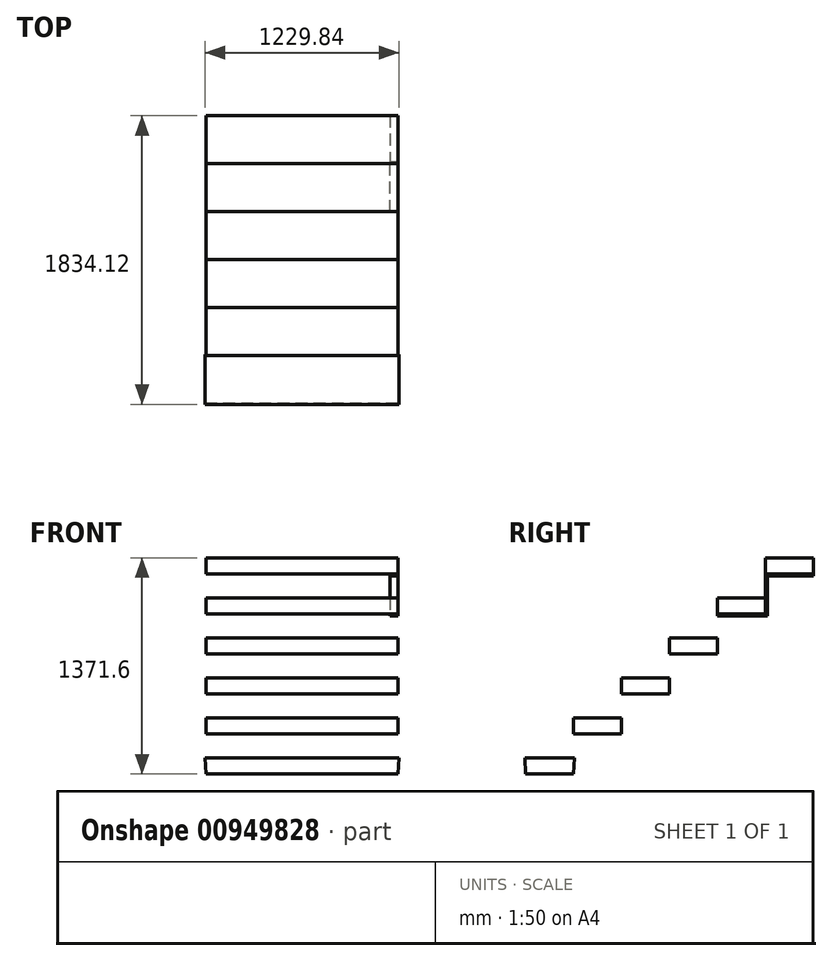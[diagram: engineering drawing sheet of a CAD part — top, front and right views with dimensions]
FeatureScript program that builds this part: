
annotation { "Feature Type Name" : "Feature", "Feature Type Description" : "" }
export const myFeature = defineFeature(function(context is Context, id is Id, definition is map)
    precondition{}
    {
        {
            var Q0;
            Q0=qCreatedBy(makeId("Top.planeOp"),FACE);
            var sketch = newSketch(context, id + "F0", { "sketchPlane" : qUnion([Q0])});
            skLineSegment(sketch, "E0.bottom", {"start": v(609.6, 152.4) * mm, "end": v(-609.6, 152.4) * mm});
            skLineSegment(sketch, "E0.top", {"start": v(609.6, -152.4) * mm, "end": v(-609.6, -152.4) * mm});
            skLineSegment(sketch, "E0.left", {"start": v(609.6, 152.4) * mm, "end": v(609.6, -152.4) * mm});
            skLineSegment(sketch, "E0.right", {"start": v(-609.6, 152.4) * mm, "end": v(-609.6, -152.4) * mm});
            skPoint(sketch, "E0.middle", {"position": v(0, 0) * mm});
            skSolve(sketch);
        }
        {
            var Q0;
            Q0 = qSketchRegion(id + "F0", true);
            extrude(context, id + "F1", {"entities" : qUnion([Q0]), "depth" : 101.6 * mm, "offsetDistance" : 25.4 * mm, "hasDraft" : true, "draftAngle" : 3 * degree});
        }
        {
            var Q0;
            Q0=makeQuery(id+"F1.opExtrude","CAP_FACE",FACE,{"disambiguationData":[OSD([sQuery(id+"F0.wireOp",EDGE,"E0.bottom"),sQuery(id+"F0.wireOp",EDGE,"E0.top"),sQuery(id+"F0.wireOp",EDGE,"E0.left"),sQuery(id+"F0.wireOp",EDGE,"E0.right")])],"isStart":false});
            cPlane(context, id + "F2", {"entities" : qUnion([Q0]), "cplaneType" : CPlaneType.OFFSET, "offset" : 152.4 * mm, "width" : 152.4 * mm, "height" : 152.4 * mm});
        }
        {
            var Q0;
            Q0=qCreatedBy(id+"F2.planeOp",FACE);
            var sketch = newSketch(context, id + "F3", { "sketchPlane" : qUnion([Q0])});
            skLineSegment(sketch, "E1.bottom", {"start": v(609.6, 457.2) * mm, "end": v(-609.6, 457.2) * mm});
            skLineSegment(sketch, "E1.top", {"start": v(609.6, 152.4) * mm, "end": v(-609.6, 152.4) * mm});
            skLineSegment(sketch, "E1.left", {"start": v(609.6, 457.2) * mm, "end": v(609.6, 152.4) * mm});
            skLineSegment(sketch, "E1.right", {"start": v(-609.6, 457.2) * mm, "end": v(-609.6, 152.4) * mm});
            skPoint(sketch, "E1.middle", {"position": v(0, 304.8) * mm});
            skSolve(sketch);
        }
        {
            var Q0;
            Q0 = qSketchRegion(id + "F3", true);
            extrude(context, id + "F4", {"entities" : qUnion([Q0]), "depth" : 101.6 * mm, "offsetDistance" : 25.4 * mm});
        }
        {
            var Q0;
            Q0=makeQuery(id+"F4.opExtrude","CAP_FACE",FACE,{"disambiguationData":[OSD([sQuery(id+"F3.wireOp",EDGE,"E1.bottom"),sQuery(id+"F3.wireOp",EDGE,"E1.top"),sQuery(id+"F3.wireOp",EDGE,"E1.left"),sQuery(id+"F3.wireOp",EDGE,"E1.right")])],"isStart":false});
            cPlane(context, id + "F5", {"entities" : qUnion([Q0]), "cplaneType" : CPlaneType.OFFSET, "offset" : 152.4 * mm, "width" : 152.4 * mm, "height" : 152.4 * mm});
        }
        {
            var Q0;
            Q0=qCreatedBy(id+"F5.planeOp",FACE);
            var sketch = newSketch(context, id + "F6", { "sketchPlane" : qUnion([Q0])});
            skLineSegment(sketch, "E2.bottom", {"start": v(609.6, 762) * mm, "end": v(-609.6, 762) * mm});
            skLineSegment(sketch, "E2.top", {"start": v(609.6, 457.2) * mm, "end": v(-609.6, 457.2) * mm});
            skLineSegment(sketch, "E2.left", {"start": v(609.6, 762) * mm, "end": v(609.6, 457.2) * mm});
            skLineSegment(sketch, "E2.right", {"start": v(-609.6, 762) * mm, "end": v(-609.6, 457.2) * mm});
            skPoint(sketch, "E2.middle", {"position": v(0, 609.6) * mm});
            skSolve(sketch);
        }
        {
            var Q0;
            Q0 = qSketchRegion(id + "F6", true);
            extrude(context, id + "F7", {"entities" : qUnion([Q0]), "depth" : 101.6 * mm, "offsetDistance" : 25.4 * mm});
        }
        {
            var Q0;
            Q0=makeQuery(id+"F7.opExtrude","CAP_FACE",FACE,{"disambiguationData":[OSD([sQuery(id+"F6.wireOp",EDGE,"E2.bottom"),sQuery(id+"F6.wireOp",EDGE,"E2.top"),sQuery(id+"F6.wireOp",EDGE,"E2.left"),sQuery(id+"F6.wireOp",EDGE,"E2.right")])],"isStart":false});
            cPlane(context, id + "F8", {"entities" : qUnion([Q0]), "cplaneType" : CPlaneType.OFFSET, "offset" : 152.4 * mm, "width" : 152.4 * mm, "height" : 152.4 * mm});
        }
        {
            var Q0;
            Q0=qCreatedBy(id+"F8.planeOp",FACE);
            var sketch = newSketch(context, id + "F9", { "sketchPlane" : qUnion([Q0])});
            skLineSegment(sketch, "E3.bottom", {"start": v(609.6, 1066.8) * mm, "end": v(-609.6, 1066.8) * mm});
            skLineSegment(sketch, "E3.top", {"start": v(609.6, 762) * mm, "end": v(-609.6, 762) * mm});
            skLineSegment(sketch, "E3.left", {"start": v(609.6, 1066.8) * mm, "end": v(609.6, 762) * mm});
            skLineSegment(sketch, "E3.right", {"start": v(-609.6, 1066.8) * mm, "end": v(-609.6, 762) * mm});
            skPoint(sketch, "E3.middle", {"position": v(0, 914.4) * mm});
            skSolve(sketch);
        }
        {
            var Q0;
            Q0=makeQuery(id+"F9.imprint","IMPRINT",FACE,{"disambiguationData":[TD([[makeQuery(id+"F9.imprint","IMPRINT",EDGE,{"derivedFrom":sQuery(id+"F9.wireOp",EDGE,"E3.bottom")}),1.0]])]});
            extrude(context, id + "F10", {"entities" : qUnion([Q0]), "depth" : 101.6 * mm, "offsetDistance" : 25.4 * mm});
        }
        {
            var Q0;
            Q0=makeQuery(id+"F10.opExtrude","CAP_FACE",FACE,{"disambiguationData":[OSD([sQuery(id+"F9.wireOp",EDGE,"E3.bottom"),sQuery(id+"F9.wireOp",EDGE,"E3.top"),sQuery(id+"F9.wireOp",EDGE,"E3.left"),sQuery(id+"F9.wireOp",EDGE,"E3.right")])],"isStart":false});
            cPlane(context, id + "F11", {"entities" : qUnion([Q0]), "cplaneType" : CPlaneType.OFFSET, "offset" : 152.4 * mm, "width" : 152.4 * mm, "height" : 152.4 * mm});
        }
        {
            var Q0;
            Q0=qCreatedBy(id+"F11.planeOp",FACE);
            var sketch = newSketch(context, id + "F12", { "sketchPlane" : qUnion([Q0])});
            skLineSegment(sketch, "E4.bottom", {"start": v(609.6, 1371.6) * mm, "end": v(-609.6, 1371.6) * mm});
            skLineSegment(sketch, "E4.top", {"start": v(609.6, 1066.8) * mm, "end": v(-609.6, 1066.8) * mm});
            skLineSegment(sketch, "E4.left", {"start": v(609.6, 1371.6) * mm, "end": v(609.6, 1066.8) * mm});
            skLineSegment(sketch, "E4.right", {"start": v(-609.6, 1371.6) * mm, "end": v(-609.6, 1066.8) * mm});
            skPoint(sketch, "E4.middle", {"position": v(0, 1219.2) * mm});
            skSolve(sketch);
        }
        {
            var Q0;
            Q0=makeQuery(id+"F12.imprint","IMPRINT",FACE,{"disambiguationData":[TD([[makeQuery(id+"F12.imprint","IMPRINT",EDGE,{"derivedFrom":sQuery(id+"F12.wireOp",EDGE,"E4.bottom")}),1.0]])]});
            extrude(context, id + "F13", {"entities" : qUnion([Q0]), "depth" : 101.6 * mm, "offsetDistance" : 25.4 * mm});
        }
        {
            var Q0;
            Q0=makeQuery(id+"F13.opExtrude","CAP_FACE",FACE,{"disambiguationData":[OSD([sQuery(id+"F12.wireOp",EDGE,"E4.bottom"),sQuery(id+"F12.wireOp",EDGE,"E4.top"),sQuery(id+"F12.wireOp",EDGE,"E4.left"),sQuery(id+"F12.wireOp",EDGE,"E4.right")])],"isStart":false});
            cPlane(context, id + "F14", {"entities" : qUnion([Q0]), "cplaneType" : CPlaneType.OFFSET, "offset" : 152.4 * mm, "width" : 152.4 * mm, "height" : 152.4 * mm});
        }
        {
            var Q0;
            Q0=qCreatedBy(id+"F14.planeOp",FACE);
            var sketch = newSketch(context, id + "F15", { "sketchPlane" : qUnion([Q0])});
            skLineSegment(sketch, "E5.bottom", {"start": v(609.6, 1676.4) * mm, "end": v(-609.6, 1676.4) * mm});
            skLineSegment(sketch, "E5.top", {"start": v(609.6, 1371.6) * mm, "end": v(-609.6, 1371.6) * mm});
            skLineSegment(sketch, "E5.left", {"start": v(609.6, 1676.4) * mm, "end": v(609.6, 1371.6) * mm});
            skLineSegment(sketch, "E5.right", {"start": v(-609.6, 1676.4) * mm, "end": v(-609.6, 1371.6) * mm});
            skPoint(sketch, "E5.middle", {"position": v(0, 1524) * mm});
            skSolve(sketch);
        }
        {
            var Q0;
            Q0=makeQuery(id+"F15.imprint","IMPRINT",FACE,{"disambiguationData":[TD([[makeQuery(id+"F15.imprint","IMPRINT",EDGE,{"derivedFrom":sQuery(id+"F15.wireOp",EDGE,"E5.bottom")}),1.0]])]});
            extrude(context, id + "F16", {"entities" : qUnion([Q0]), "depth" : 101.6 * mm, "offsetDistance" : 25.4 * mm});
        }
        {
            var Q0;
            Q0=makeQuery(id+"F16.opExtrude","SWEPT_FACE",FACE,{"disambiguationData":[OSD([sQuery(id+"F15.wireOp",EDGE,"E5.top")])]});
            cPlane(context, id + "F17", {"entities" : qUnion([Q0]), "cplaneType" : CPlaneType.OFFSET, "offset" : 0 * mm, "width" : 152.4 * mm, "height" : 152.4 * mm});
        }
        {
            var Q0;
            Q0=qCreatedBy(id+"F17.planeOp",FACE);
            var sketch = newSketch(context, id + "F18", { "sketchPlane" : qUnion([Q0])});
            skLineSegment(sketch, "E6.bottom", {"start": v(558.8, 1257.3) * mm, "end": v(609.6, 1257.3) * mm});
            skLineSegment(sketch, "E6.top", {"start": v(558.8, 1016) * mm, "end": v(609.6, 1016) * mm});
            skLineSegment(sketch, "E6.left", {"start": v(558.8, 1257.3) * mm, "end": v(558.8, 1016) * mm});
            skLineSegment(sketch, "E6.right", {"start": v(609.6, 1257.3) * mm, "end": v(609.6, 1016) * mm});
            skSolve(sketch);
        }
        {
            var Q0;
            Q0 = qSketchRegion(id + "F18", true);
            extrude(context, id + "F19", {"entities" : qUnion([Q0]), "oppositeDirection" : true, "depth" : 12.7 * mm, "offsetDistance" : 25.4 * mm});
        }
        {
            var Q0;
            Q0=qCreatedBy(id+"F14.planeOp",FACE);
            var sketch = newSketch(context, id + "F20", { "sketchPlane" : qUnion([Q0])});
            skLineSegment(sketch, "E7.bottom", {"start": v(609.6, 1676.4) * mm, "end": v(558.8, 1676.4) * mm});
            skLineSegment(sketch, "E7.top", {"start": v(609.6, 1371.6) * mm, "end": v(558.8, 1371.6) * mm});
            skLineSegment(sketch, "E7.left", {"start": v(609.6, 1676.4) * mm, "end": v(609.6, 1371.6) * mm});
            skLineSegment(sketch, "E7.right", {"start": v(558.8, 1676.4) * mm, "end": v(558.8, 1371.6) * mm});
            skSolve(sketch);
        }
        {
            var Q0;
            Q0=makeQuery(id+"F20.imprint","IMPRINT",FACE,{"disambiguationData":[TD([[makeQuery(id+"F20.imprint","IMPRINT",EDGE,{"derivedFrom":sQuery(id+"F20.wireOp",EDGE,"E7.bottom")}),1.0]])]});
            extrude(context, id + "F21", {"entities" : qUnion([Q0]), "oppositeDirection" : true, "depth" : 12.7 * mm, "offsetDistance" : 25.4 * mm});
        }
        {
            var Q0;
            Q0=qCreatedBy(id+"F11.planeOp",FACE);
            var sketch = newSketch(context, id + "F22", { "sketchPlane" : qUnion([Q0])});
            skLineSegment(sketch, "E8.bottom", {"start": v(609.6, 1066.8) * mm, "end": v(558.8, 1066.8) * mm});
            skLineSegment(sketch, "E8.top", {"start": v(609.6, 1384.3) * mm, "end": v(558.8, 1384.3) * mm});
            skLineSegment(sketch, "E8.left", {"start": v(609.6, 1066.8) * mm, "end": v(609.6, 1384.3) * mm});
            skLineSegment(sketch, "E8.right", {"start": v(558.8, 1066.8) * mm, "end": v(558.8, 1384.3) * mm});
            skSolve(sketch);
        }
        {
            var Q0;
            Q0 = qSketchRegion(id + "F22", true);
            extrude(context, id + "F23", {"entities" : qUnion([Q0]), "oppositeDirection" : true, "depth" : 12.7 * mm, "offsetDistance" : 25.4 * mm});
        }
    });
